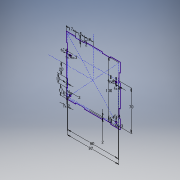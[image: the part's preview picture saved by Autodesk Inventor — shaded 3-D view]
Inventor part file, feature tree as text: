
AUTODESK INVENTOR PART (.ipt)
format: ipt  version: 2016 (Build 200138000, 138)  size: 166,912 bytes
history: native  units: mm
features: other x1, extrude x1, sketch x1
ambient origin geometry x8: Origin, YZ Plane, XZ Plane, XY Plane, X Axis, Y Axis, Z Axis, Center Point
bodies: Body1 (feature_tree)
feature tree (3):
  other  "ソリッド1"
  extrude  "押し出し1"  Depth=92.0mm
  sketch  "スケッチ1"
